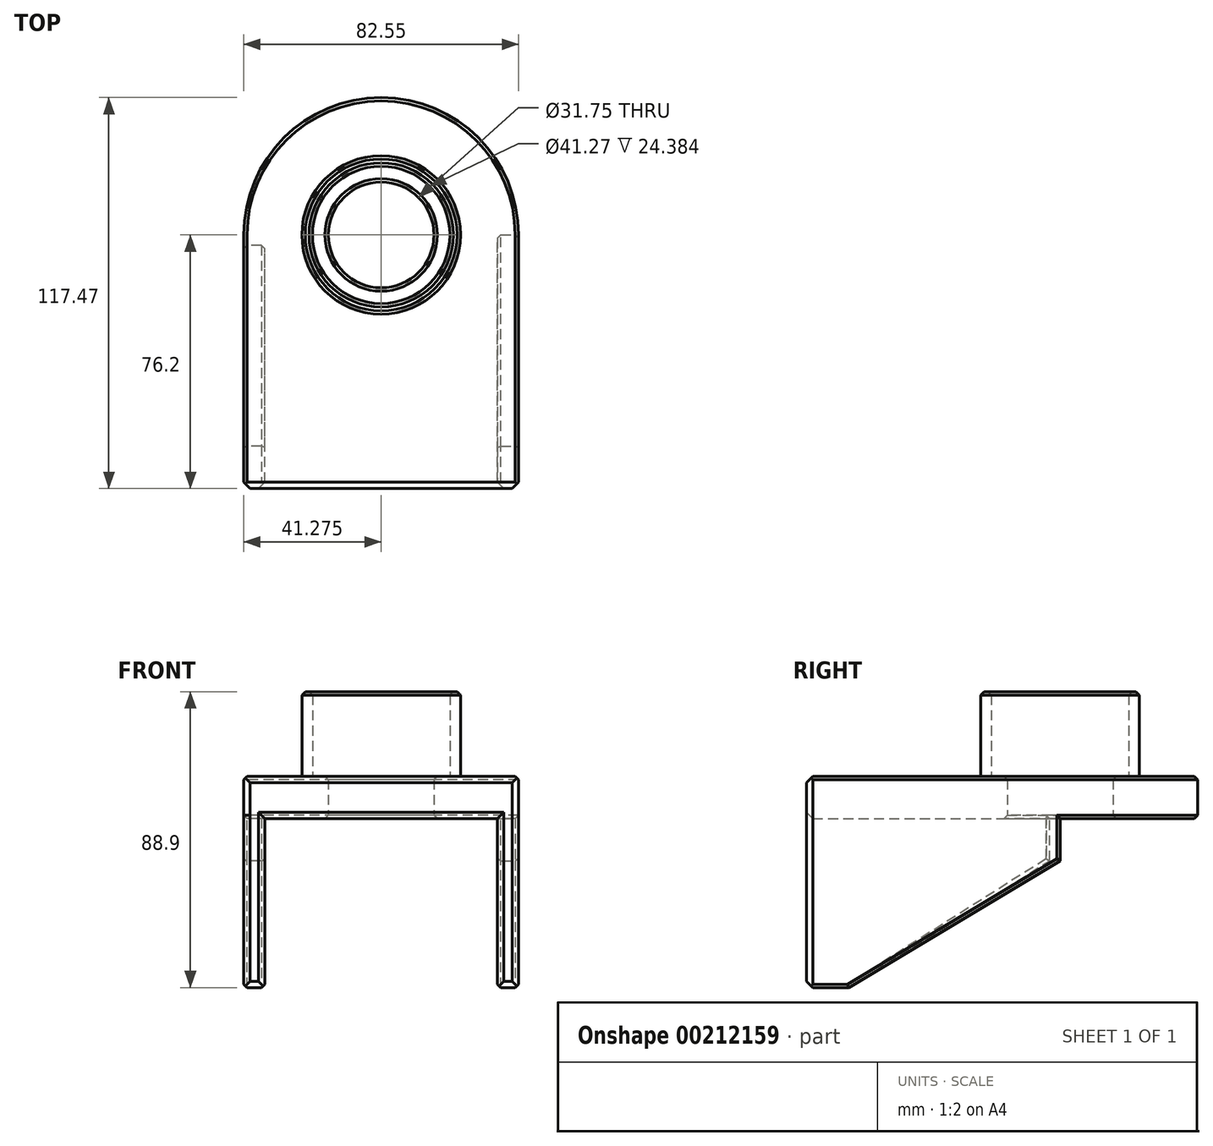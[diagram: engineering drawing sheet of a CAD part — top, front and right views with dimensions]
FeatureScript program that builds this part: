
annotation { "Feature Type Name" : "Feature", "Feature Type Description" : "" }
export const myFeature = defineFeature(function(context is Context, id is Id, definition is map)
    precondition{}
    {
        {
            var Q0;
            Q0=qCreatedBy(makeId("Top.planeOp"),FACE);
            var sketch = newSketch(context, id + "F0", { "sketchPlane" : qUnion([Q0])});
            skLineSegment(sketch, "E0.bottom", {"start": v(0, 0) * mm, "end": v(82.55, 0) * mm});
            skLineSegment(sketch, "E0.top", {"start": v(41.27, 117.48) * mm, "end": v(41.28, 117.48) * mm});
            skLineSegment(sketch, "E0.left", {"start": v(0, 0) * mm, "end": v(0, 76.2) * mm});
            skLineSegment(sketch, "E0.right", {"start": v(82.55, 0) * mm, "end": v(82.55, 76.2) * mm});
            skPoint(sketch, "E1.visualSharp", {"position": v(0, 117.48) * mm});
            skArc(sketch, "E1.filletArc", {"start": v(41.27, 117.48) * mm, "mid": v(12.09, 105.39) * mm, "end": v(0, 76.2) * mm});
            skPoint(sketch, "E2.visualSharp", {"position": v(82.55, 117.48) * mm});
            skArc(sketch, "E2.filletArc", {"start": v(82.55, 76.2) * mm, "mid": v(70.46, 105.39) * mm, "end": v(41.28, 117.48) * mm});
            skCircle(sketch, "E3", {"center": v(41.27, 76.2) * mm, "radius": 15.88 * mm});
            skSolve(sketch);
        }
        {
            var Q0;
            Q0=makeQuery(id+"F0.imprint","IMPRINT",FACE,{"disambiguationData":[TD([[makeQuery(id+"F0.imprint","IMPRINT",EDGE,{"derivedFrom":sQuery(id+"F0.wireOp",EDGE,"E0.bottom")}),1.0]])]});
            extrude(context, id + "F1", {"entities" : qUnion([Q0]), "depth" : 12.7 * mm});
        }
        {
            var Q0;
            Q0=makeQuery(id+"F1.opExtrude","CAP_FACE",FACE,{"disambiguationData":[OSD([sQuery(id+"F0.wireOp",EDGE,"E0.bottom"),sQuery(id+"F0.wireOp",EDGE,"E0.left"),sQuery(id+"F0.wireOp",EDGE,"E0.right"),sQuery(id+"F0.wireOp",EDGE,"E1.filletArc"),sQuery(id+"F0.wireOp",EDGE,"E2.filletArc"),sQuery(id+"F0.wireOp",EDGE,"E3")])],"isStart":false});
            var sketch = newSketch(context, id + "F2", { "sketchPlane" : qUnion([Q0])});
            skCircle(sketch, "E4", {"center": v(41.28, 76.2) * mm, "radius": 20.64 * mm});
            skCircle(sketch, "E5", {"center": v(41.28, 76.2) * mm, "radius": 23.81 * mm});
            skSolve(sketch);
        }
        {
            var Q0;
            Q0=makeQuery(id+"F2.imprint","IMPRINT",FACE,{"disambiguationData":[TD([[makeQuery(id+"F2.imprint","IMPRINT",EDGE,{"derivedFrom":sQuery(id+"F2.wireOp",EDGE,"E4")}),-1.0]])]});
            extrude(context, id + "F3", {"entities" : qUnion([Q0]), "operationType" : NewBodyOperationType.ADD, "depth" : 25.4 * mm});
        }
        {
            var Q0;
            Q0=makeQuery(id+"F1.opExtrude","SWEPT_FACE",FACE,{"disambiguationData":[OSD([sQuery(id+"F0.wireOp",EDGE,"E0.left")])]});
            var sketch = newSketch(context, id + "F4", { "sketchPlane" : qUnion([Q0])});
            skLineSegment(sketch, "E6", {"start": v(0, -50.8) * mm, "end": v(0, 0) * mm});
            skLineSegment(sketch, "E7.MirrorCS", {"start": v(-12.7, -50.8) * mm, "end": v(0, -50.8) * mm});
            skLineSegment(sketch, "E8.MirrorCS", {"start": v(0, 0) * mm, "end": v(-73.03, 0) * mm});
            skLineSegment(sketch, "E9", {"start": v(-73.03, 0) * mm, "end": v(-73.03, -12.7) * mm});
            skLineSegment(sketch, "E10", {"start": v(-73.03, -12.7) * mm, "end": v(-12.7, -50.8) * mm});
            skSolve(sketch);
        }
        {
            var Q0;
            {var subQ4=sQuery(id+"F4.wireOp",EDGE,"E6");Q0=makeQuery(id+"F4.imprint","IMPRINT",FACE,{"disambiguationData":[TD([[makeQuery(id+"F4.imprint","IMPRINT",EDGE,{"derivedFrom":subQ4}),1.0]])]});}
            extrude(context, id + "F5", {"entities" : qUnion([Q0]), "operationType" : NewBodyOperationType.ADD, "oppositeDirection" : true, "depth" : 6.35 * mm});
        }
        {
            var Q0;
            Q0=makeQuery(id+"F1.opExtrude","SWEPT_FACE",FACE,{"disambiguationData":[OSD([sQuery(id+"F0.wireOp",EDGE,"E0.right")])]});
            var sketch = newSketch(context, id + "F6", { "sketchPlane" : qUnion([Q0])});
            skLineSegment(sketch, "E11", {"start": v(0, 0) * mm, "end": v(0, -50.8) * mm});
            skLineSegment(sketch, "E12", {"start": v(0, -50.8) * mm, "end": v(12.7, -50.8) * mm});
            skLineSegment(sketch, "E13", {"start": v(76.2, 0) * mm, "end": v(0, 0) * mm});
            skLineSegment(sketch, "E14", {"start": v(76.2, 0) * mm, "end": v(76.2, -12.7) * mm});
            skLineSegment(sketch, "E15", {"start": v(76.2, -12.7) * mm, "end": v(12.7, -50.8) * mm});
            skSolve(sketch);
        }
        {
            var Q0;
            Q0=makeQuery(id+"F6.imprint","IMPRINT",FACE,{"disambiguationData":[TD([[makeQuery(id+"F6.imprint","IMPRINT",EDGE,{"derivedFrom":sQuery(id+"F6.wireOp",EDGE,"E11")}),1.0]])]});
            extrude(context, id + "F7", {"entities" : qUnion([Q0]), "operationType" : NewBodyOperationType.ADD, "oppositeDirection" : true, "depth" : 6.35 * mm});
        }
        {
            var Q0;
            Q0=makeQuery(id+"F7.boolean.opBoolean","MERGE",FACE,{"derivedFrom":[makeQuery(id+"F5.boolean.opBoolean","MERGE",FACE,{"derivedFrom":[makeQuery(id+"F1.opExtrude","SWEPT_FACE",FACE,{"disambiguationData":[OSD([sQuery(id+"F0.wireOp",EDGE,"E0.bottom")])]}),makeQuery(id+"F5.opExtrude","SWEPT_FACE",FACE,{"disambiguationData":[OSD([sQuery(id+"F4.wireOp",EDGE,"E6")])]})]}),makeQuery(id+"F7.opExtrude","SWEPT_FACE",FACE,{"disambiguationData":[OSD([sQuery(id+"F6.wireOp",EDGE,"E11")])]})]});
            chamfer(context, id + "F8", {"entities" : qUnion([Q0]), "width" : 1.9 * mm, "tangentPropagation" : true});
        }
        {
            var Q0;
            Q0=makeQuery(id+"F7.opExtrude","CAP_EDGE",EDGE,{"disambiguationData":[OSD([sQuery(id+"F6.wireOp",EDGE,"E15")])],"isStart":true});
            var Q1;
            Q1=makeQuery(id+"F7.opExtrude","CAP_EDGE",EDGE,{"disambiguationData":[OSD([sQuery(id+"F6.wireOp",EDGE,"E14")])],"isStart":true});
            var Q2;
            Q2=makeQuery(id+"F7.opExtrude","CAP_EDGE",EDGE,{"disambiguationData":[OSD([sQuery(id+"F6.wireOp",EDGE,"E14")])],"isStart":false});
            var Q3;
            Q3=makeQuery(id+"F7.opExtrude","CAP_EDGE",EDGE,{"disambiguationData":[OSD([sQuery(id+"F6.wireOp",EDGE,"E15")])],"isStart":false});
            var Q4;
            Q4=makeQuery(id+"F7.opExtrude","CAP_EDGE",EDGE,{"disambiguationData":[OSD([sQuery(id+"F6.wireOp",EDGE,"E12")])],"isStart":false});
            var Q5;
            Q5=makeQuery(id+"F7.opExtrude","CAP_EDGE",EDGE,{"disambiguationData":[OSD([sQuery(id+"F6.wireOp",EDGE,"E12")])],"isStart":true});
            var Q6;
            Q6=makeQuery(id+"F1.opExtrude","CAP_EDGE",EDGE,{"disambiguationData":[OSD([sQuery(id+"F0.wireOp",EDGE,"E1.filletArc"),sQuery(id+"F0.wireOp",EDGE,"E2.filletArc")])],"isStart":true});
            var Q7;
            Q7=makeQuery(id+"F1.opExtrude","CAP_EDGE",EDGE,{"disambiguationData":[OSD([sQuery(id+"F0.wireOp",EDGE,"E3")])],"isStart":true});
            var Q8;
            Q8=makeQuery(id+"F5.opExtrude","CAP_EDGE",EDGE,{"disambiguationData":[OSD([sQuery(id+"F4.wireOp",EDGE,"E9")])],"isStart":false});
            var Q9;
            Q9=makeQuery(id+"F5.opExtrude","CAP_EDGE",EDGE,{"disambiguationData":[OSD([sQuery(id+"F4.wireOp",EDGE,"E10")])],"isStart":false});
            var Q10;
            Q10=makeQuery(id+"F5.opExtrude","CAP_EDGE",EDGE,{"disambiguationData":[OSD([sQuery(id+"F4.wireOp",EDGE,"E7.MirrorCS")])],"isStart":false});
            var Q11;
            Q11=makeQuery(id+"F5.opExtrude","CAP_EDGE",EDGE,{"disambiguationData":[OSD([sQuery(id+"F4.wireOp",EDGE,"E7.MirrorCS")])],"isStart":true});
            var Q12;
            Q12=makeQuery(id+"F5.opExtrude","CAP_EDGE",EDGE,{"disambiguationData":[OSD([sQuery(id+"F4.wireOp",EDGE,"E10")])],"isStart":true});
            var Q13;
            Q13=makeQuery(id+"F5.opExtrude","CAP_EDGE",EDGE,{"disambiguationData":[OSD([sQuery(id+"F4.wireOp",EDGE,"E9")])],"isStart":true});
            var Q14;
            Q14=makeQuery(id+"F1.opExtrude","CAP_EDGE",EDGE,{"disambiguationData":[OSD([sQuery(id+"F0.wireOp",EDGE,"E1.filletArc"),sQuery(id+"F0.wireOp",EDGE,"E2.filletArc")])],"isStart":false});
            var Q15;
            Q15=makeQuery(id+"F3.opExtrude","CAP_EDGE",EDGE,{"disambiguationData":[OSD([sQuery(id+"F2.wireOp",EDGE,"E5")])],"isStart":false});
            var Q16;
            Q16=makeQuery(id+"F3.opExtrude","CAP_EDGE",EDGE,{"disambiguationData":[OSD([sQuery(id+"F2.wireOp",EDGE,"E4")])],"isStart":false});
            var Q17;
            Q17=makeQuery(id+"F1.opExtrude","CAP_EDGE",EDGE,{"disambiguationData":[OSD([sQuery(id+"F0.wireOp",EDGE,"E3")])],"isStart":false});
            chamfer(context, id + "F9", {"entities" : qUnion([Q0, Q1, Q2, Q3, Q4, Q5, Q6, Q7, Q8, Q9, Q10, Q11, Q12, Q13, Q14, Q15, Q16, Q17]), "width" : 1.02 * mm, "tangentPropagation" : true});
        }
        {
            var Q0;
            Q0=makeQuery(id+"F7.boolean.opBoolean","MERGE",FACE,{"derivedFrom":[makeQuery(id+"F5.boolean.opBoolean","MERGE",FACE,{"derivedFrom":[makeQuery(id+"F1.opExtrude","SWEPT_FACE",FACE,{"disambiguationData":[OSD([sQuery(id+"F0.wireOp",EDGE,"E0.bottom")])]}),makeQuery(id+"F5.opExtrude","SWEPT_FACE",FACE,{"disambiguationData":[OSD([sQuery(id+"F4.wireOp",EDGE,"E6")])]})]}),makeQuery(id+"F7.opExtrude","SWEPT_FACE",FACE,{"disambiguationData":[OSD([sQuery(id+"F6.wireOp",EDGE,"E11")])]})]});
            var sketch = newSketch(context, id + "F10", { "sketchPlane" : qUnion([Q0])});
            skLineSegment(sketch, "E16", {"start": v(41.28, 0) * mm, "end": v(41.28, -51.2) * mm, "construction": true});
            skLineSegment(sketch, "E17.0", {"start": v(78.1, 0) * mm, "end": v(4.45, 0) * mm, "construction": true});
            skSolve(sketch);
        }
    });
